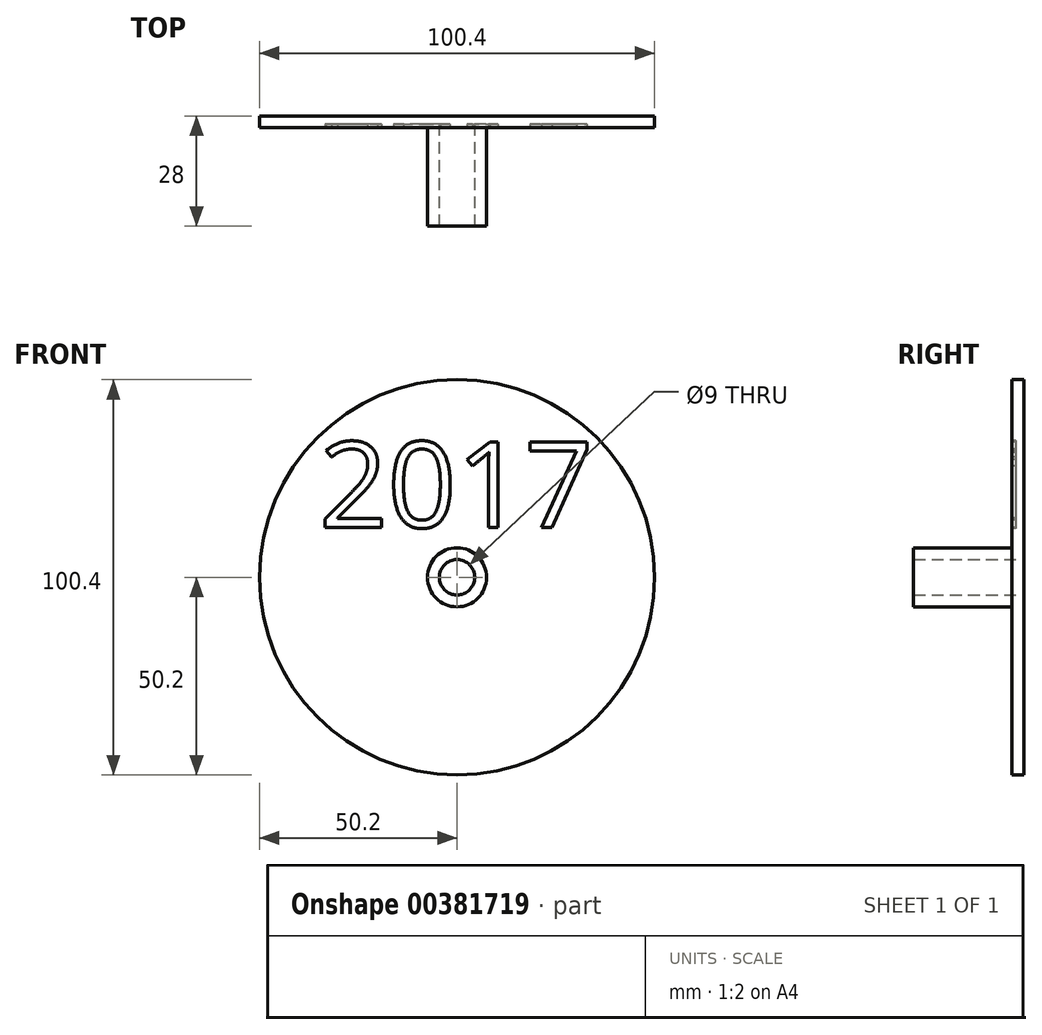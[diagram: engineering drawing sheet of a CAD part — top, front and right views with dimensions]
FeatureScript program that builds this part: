
annotation { "Feature Type Name" : "Feature", "Feature Type Description" : "" }
export const myFeature = defineFeature(function(context is Context, id is Id, definition is map)
    precondition{}
    {
        {
            var Q0;
            Q0=qCreatedBy(makeId("Front.planeOp"),FACE);
            var sketch = newSketch(context, id + "F0", { "sketchPlane" : qUnion([Q0])});
            skCircle(sketch, "E0", {"center": v(0, 0) * mm, "radius": 4.5 * mm});
            skCircle(sketch, "E1", {"center": v(0, 0) * mm, "radius": 50.2 * mm});
            skSolve(sketch);
        }
        {
            var Q0;
            Q0 = qSketchRegion(id + "F0", true);
            extrude(context, id + "F1", {"entities" : qUnion([Q0]), "depth" : 3 * mm});
        }
        {
            var Q0;
            Q0=makeQuery(id+"F1.opExtrude","CAP_FACE",FACE,{"disambiguationData":[OSD([sQuery(id+"F0.wireOp",EDGE,"E0"),sQuery(id+"F0.wireOp",EDGE,"E1")])],"isStart":false});
            var sketch = newSketch(context, id + "F2", { "sketchPlane" : qUnion([Q0])});
            skCircle(sketch, "E2", {"center": v(0, 0) * mm, "radius": 7.5 * mm});
            skCircle(sketch, "E3", {"center": v(0, 0) * mm, "radius": 4.5 * mm});
            skSolve(sketch);
        }
        {
            var Q0;
            Q0 = qSketchRegion(id + "F2", true);
            extrude(context, id + "F3", {"entities" : qUnion([Q0]), "operationType" : NewBodyOperationType.ADD, "depth" : 25 * mm});
        }
        {
            var Q0;
            Q0=makeQuery(id+"F1.opExtrude","CAP_FACE",FACE,{"disambiguationData":[OSD([sQuery(id+"F0.wireOp",EDGE,"E0"),sQuery(id+"F0.wireOp",EDGE,"E1")])],"isStart":false});
            var sketch = newSketch(context, id + "F4", { "sketchPlane" : qUnion([Q0])});
            skText(sketch, "E4", { "text": "2017", "fontName": "OpenSans-Regular.ttf"});
            const initialGuessF4  = {"E4": [-0.035, 0.01268, 1, 0, 0.0219]};
            skSetInitialGuess(sketch, initialGuessF4);
            skSolve(sketch);
        }
        {
            var Q0;
            Q0 = qSketchRegion(id + "F4", true);
            extrude(context, id + "F5", {"entities" : qUnion([Q0]), "operationType" : NewBodyOperationType.REMOVE, "oppositeDirection" : true, "depth" : 1 * mm});
        }
    });
